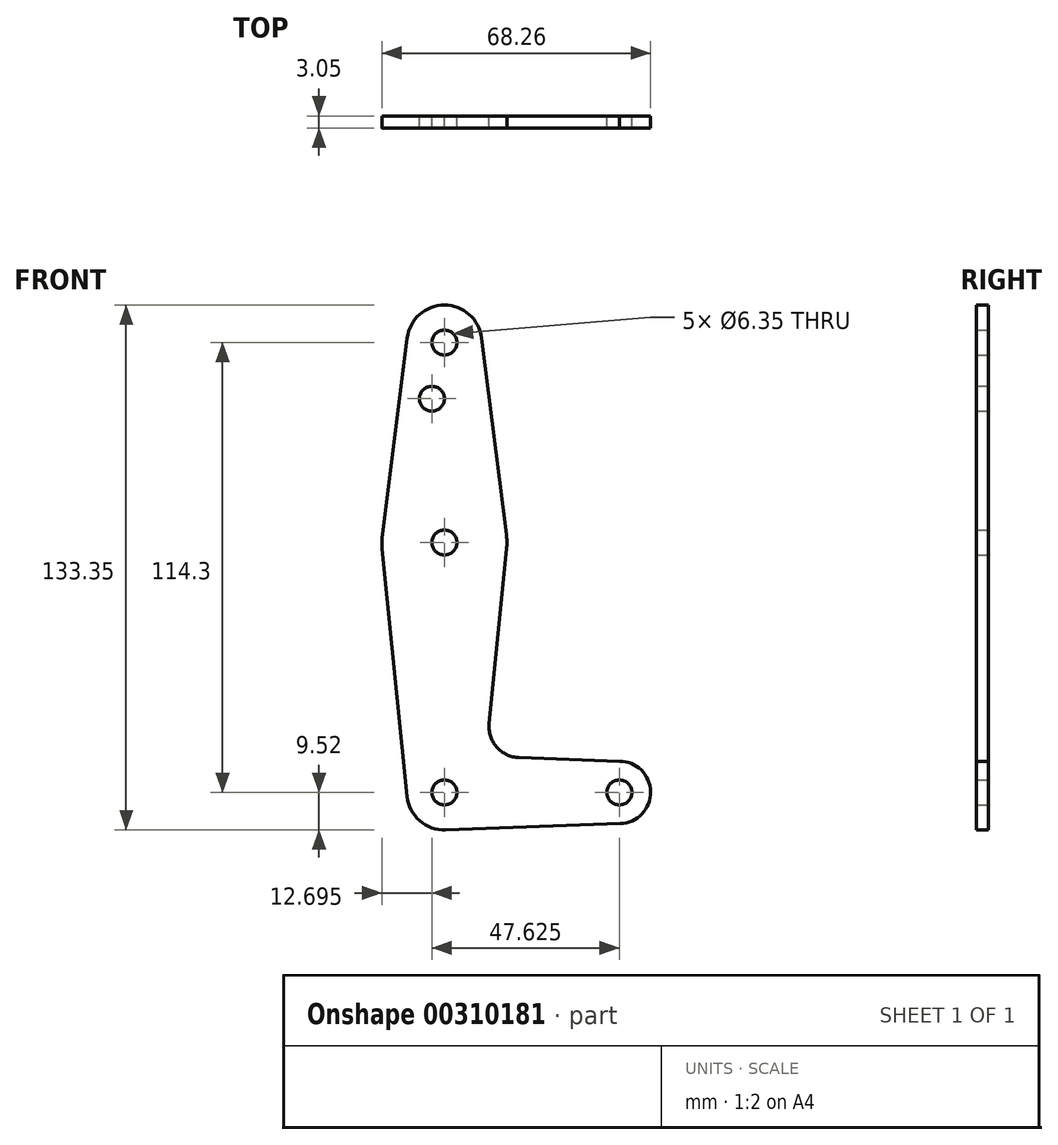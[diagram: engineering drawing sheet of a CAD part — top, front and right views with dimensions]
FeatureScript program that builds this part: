
annotation { "Feature Type Name" : "Feature", "Feature Type Description" : "" }
export const myFeature = defineFeature(function(context is Context, id is Id, definition is map)
    precondition{}
    {
        {
            var Q0;
            Q0=qCreatedBy(makeId("Front.planeOp"),FACE);
            var sketch = newSketch(context, id + "F0", { "sketchPlane" : qUnion([Q0])});
            skLineSegment(sketch, "E0", {"start": v(0, 0) * mm, "end": v(0, 114.3) * mm, "construction": true});
            skLineSegment(sketch, "E1", {"start": v(0, 0) * mm, "end": v(44.45, 0) * mm, "construction": true});
            skCircle(sketch, "E2", {"center": v(0, 114.3) * mm, "radius": 9.53 * mm});
            skCircle(sketch, "E3", {"center": v(0, 63.5) * mm, "radius": 15.88 * mm});
            skCircle(sketch, "E4", {"center": v(0, 0) * mm, "radius": 9.53 * mm});
            skCircle(sketch, "E5", {"center": v(44.45, 0) * mm, "radius": 7.94 * mm});
            skLineSegment(sketch, "E6", {"start": v(9.45, 115.5) * mm, "end": v(15.75, 65.48) * mm});
            skLineSegment(sketch, "E7", {"start": v(-9.45, 115.5) * mm, "end": v(-15.75, 65.48) * mm});
            skLineSegment(sketch, "E8", {"start": v(-15.8, 61.91) * mm, "end": v(-9.48, -0.95) * mm});
            skLineSegment(sketch, "E9", {"start": v(15.8, 61.91) * mm, "end": v(11.34, 17.6) * mm});
            skLineSegment(sketch, "E10", {"start": v(44.45, 7.94) * mm, "end": v(18.97, 8.85) * mm});
            skLineSegment(sketch, "E11", {"start": v(0.34, -9.52) * mm, "end": v(44.73, -7.93) * mm});
            skCircle(sketch, "E12", {"center": v(0, 114.3) * mm, "radius": 3.18 * mm});
            skCircle(sketch, "E13", {"center": v(-3.17, 100.03) * mm, "radius": 3.18 * mm});
            skCircle(sketch, "E14", {"center": v(0, 63.5) * mm, "radius": 3.18 * mm});
            skCircle(sketch, "E15", {"center": v(0, 0) * mm, "radius": 3.18 * mm});
            skCircle(sketch, "E16", {"center": v(44.45, 0) * mm, "radius": 3.18 * mm});
            skArc(sketch, "E17.filletArc", {"start": v(11.34, 17.6) * mm, "mid": v(13.26, 11.57) * mm, "end": v(18.97, 8.85) * mm});
            skSolve(sketch);
        }
        {
            var Q0;
            Q0 = qSketchRegion(id + "F0", true);
            extrude(context, id + "F1", {"entities" : qUnion([Q0]), "depth" : 3.05 * mm});
        }
    });
